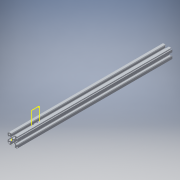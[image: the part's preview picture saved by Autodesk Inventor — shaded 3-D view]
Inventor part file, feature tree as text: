
AUTODESK INVENTOR PART (.ipt)
format: ipt  version: 2017 (Build 210142000, 142)  size: 459,264 bytes
history: native  units: in
note: dims shown in document units (in); Inventor stores cm internally (conversion verified against a paired STEP export)
features: sketch x4, extrude x3, other x3, reference x2, fillet x1
ambient origin geometry x8: Origin, YZ Plane, XZ Plane, XY Plane, X Axis, Y Axis, Z Axis, Center Point
bodies: Solid1 (feature_tree)
feature tree (13):
  extrude  "Extrusion1"  Depth=1.0in TaperAngle=0.0deg
  sketch  "Sketch3"  dims[d7=1.5in d8=0.0in]
  extrude  "Extrusion2"  [1 undecoded]
  extrude  "Extrusion3"  [1 undecoded]
  sketch  "Sketch2"  dims[d0=57.0in d1=0.0in d5=1.0in d6=0.0in]
  sketch  "Sketch4"
  reference  "Reference1"
  sketch  "Sketch5"
  reference  "Reference2"
  fillet  "Fillet10"  [1 undecoded]
  other  "Robot Frame '16.iam"
  other  "Inline Cylinder Mount Bracket:1"
  other  "Inline Cylinder Mount Bracket:2"
note: 3 required parameter values undecoded (feature->parameter linkage not recoverable at this tier; creation-order binding heuristic only, values carry confidence <= 0.55)
